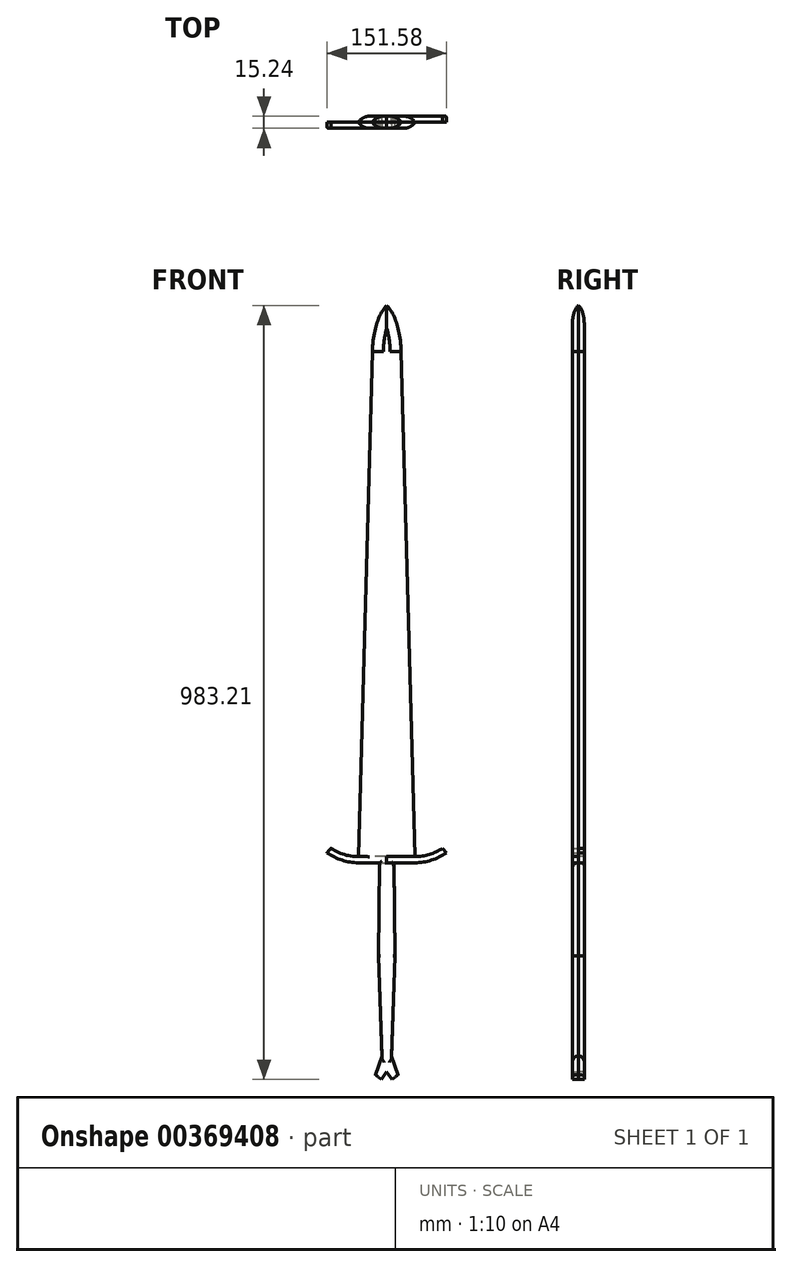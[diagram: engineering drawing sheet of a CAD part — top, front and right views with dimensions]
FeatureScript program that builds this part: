
annotation { "Feature Type Name" : "Feature", "Feature Type Description" : "" }
export const myFeature = defineFeature(function(context is Context, id is Id, definition is map)
    precondition{}
    {
        {
            var Q0;
            Q0=qCreatedBy(makeId("Front.planeOp"),FACE);
            var sketch = newSketch(context, id + "F0", { "sketchPlane" : qUnion([Q0])});
            skLineSegment(sketch, "E0", {"start": v(0, -570.47) * mm, "end": v(0, 382.75) * mm});
            skFitSpline(sketch, "E1", {"points": [v(0, 382.75) * mm, v(-11.14, 364.34) * mm, v(-18.35, 324.36) * mm], "startDerivative": vector(-35, -40.1) * mm, "endDerivative": vector(-2.28, -78.56) * mm});
            skLineSegment(sketch, "E2", {"start": v(-18.35, 324.36) * mm, "end": v(-35.93, -317.64) * mm});
            skLineSegment(sketch, "E3", {"start": v(0, -317.64) * mm, "end": v(-35.93, -317.64) * mm});
            skArc(sketch, "E4", {"start": v(-70.75, -306.94) * mm, "mid": v(-54.15, -314.9) * mm, "end": v(-35.93, -317.64) * mm});
            skLineSegment(sketch, "E5", {"start": v(-70.75, -306.94) * mm, "end": v(-75.79, -312.66) * mm});
            skLineSegment(sketch, "E6", {"start": v(0, -317.64) * mm, "end": v(0, -325.65) * mm});
            skArc(sketch, "E7", {"start": v(-75.79, -312.66) * mm, "mid": v(-56.83, -322.07) * mm, "end": v(-35.93, -325.43) * mm});
            skLineSegment(sketch, "E8", {"start": v(-35.93, -325.43) * mm, "end": v(0, -325.65) * mm});
            skLineSegment(sketch, "E9", {"start": v(-9.27, -325.6) * mm, "end": v(-10.18, -443.7) * mm});
            skLineSegment(sketch, "E10", {"start": v(-10.18, -443.7) * mm, "end": v(-6.03, -571.22) * mm});
            skLineSegment(sketch, "E11.MirrorCS", {"start": v(10.18, -443.7) * mm, "end": v(6.03, -571.22) * mm});
            skLineSegment(sketch, "E12.MirrorCS", {"start": v(9.27, -325.6) * mm, "end": v(10.18, -443.7) * mm});
            skLineSegment(sketch, "E13.MirrorCS", {"start": v(35.93, -325.43) * mm, "end": v(0, -325.65) * mm});
            skLineSegment(sketch, "E14.MirrorCS", {"start": v(0, -317.64) * mm, "end": v(35.93, -317.64) * mm});
            skLineSegment(sketch, "E15.MirrorCS", {"start": v(18.35, 324.36) * mm, "end": v(35.93, -317.64) * mm});
            skArc(sketch, "E16.MirrorCS", {"start": v(75.79, -312.66) * mm, "mid": v(56.83, -322.07) * mm, "end": v(35.93, -325.43) * mm});
            skArc(sketch, "E17.MirrorCS", {"start": v(70.75, -306.94) * mm, "mid": v(54.15, -314.9) * mm, "end": v(35.93, -317.64) * mm});
            skFitSpline(sketch, "E18.MirrorCS", {"points": [v(0, 382.75) * mm, v(11.14, 364.34) * mm, v(18.35, 324.36) * mm], "startDerivative": vector(35, -40.1) * mm, "endDerivative": vector(2.28, -78.56) * mm});
            skLineSegment(sketch, "E19", {"start": v(-6.03, -571.22) * mm, "end": v(-14.6, -594.67) * mm});
            skLineSegment(sketch, "E20", {"start": v(-14.6, -594.67) * mm, "end": v(-6.81, -600.46) * mm});
            skLineSegment(sketch, "E21", {"start": v(-6.81, -600.46) * mm, "end": v(0, -591.3) * mm});
            skLineSegment(sketch, "E22.MirrorCS", {"start": v(6.03, -571.22) * mm, "end": v(14.6, -594.67) * mm});
            skLineSegment(sketch, "E23.MirrorCS", {"start": v(14.6, -594.67) * mm, "end": v(6.81, -600.46) * mm});
            skLineSegment(sketch, "E24.MirrorCS", {"start": v(6.81, -600.46) * mm, "end": v(0, -591.3) * mm});
            skLineSegment(sketch, "E25.MirrorCS", {"start": v(70.75, -306.94) * mm, "end": v(75.79, -312.66) * mm});
            skSolve(sketch);
        }
        {
            var Q0;
            {var subQ0=sQuery(id+"F0.wireOp",EDGE,"E1");Q0=makeQuery(id+"F0.imprint","IMPRINT",FACE,{"disambiguationData":[TD([[makeQuery(id+"F0.imprint","IMPRINT",EDGE,{"derivedFrom":subQ0}),1.0]])]});}
            var Q1;
            {var subQ2=sQuery(id+"F0.wireOp",EDGE,"E14.MirrorCS");Q1=makeQuery(id+"F0.imprint","IMPRINT",FACE,{"disambiguationData":[TD([[makeQuery(id+"F0.imprint","IMPRINT",EDGE,{"derivedFrom":subQ2}),1.0]])]});}
            var Q2;
            Q2=makeQuery(id+"F0.imprint","IMPRINT",FACE,{"disambiguationData":[TD([[makeQuery(id+"F0.imprint","IMPRINT",EDGE,{"derivedFrom":sQuery(id+"F0.wireOp",EDGE,"E3")}),1.0]])]});
            var Q3;
            {var subQ1=sQuery(id+"F0.wireOp",EDGE,"E6");Q3=makeQuery(id+"F0.imprint","IMPRINT",FACE,{"disambiguationData":[TD([[makeQuery(id+"F0.imprint","IMPRINT",EDGE,{"derivedFrom":subQ1}),1.0]])]});}
            var Q4;
            {var subQ4=sQuery(id+"F0.wireOp",EDGE,"E9");Q4=makeQuery(id+"F0.imprint","IMPRINT",FACE,{"disambiguationData":[TD([[makeQuery(id+"F0.imprint","IMPRINT",EDGE,{"derivedFrom":subQ4}),1.0]])]});}
            extrude(context, id + "F1", {"entities" : qUnion([Q0, Q1, Q2, Q3, Q4]), "depth" : 7.62 * mm});
        }
        {
            var Q0;
            Q0=makeQuery(id+"F1.opExtrude","CAP_EDGE",EDGE,{"disambiguationData":[OSD([sQuery(id+"F0.wireOp",EDGE,"E15.MirrorCS")])],"isStart":false});
            var Q1;
            Q1=makeQuery(id+"F1.opExtrude","CAP_EDGE",EDGE,{"disambiguationData":[OSD([sQuery(id+"F0.wireOp",EDGE,"E2")])],"isStart":false});
            var Q2;
            Q2=makeQuery(id+"F1.opExtrude","CAP_EDGE",EDGE,{"disambiguationData":[OSD([sQuery(id+"F0.wireOp",EDGE,"E1")])],"isStart":false});
            var Q3;
            Q3=makeQuery(id+"F1.opExtrude","CAP_EDGE",EDGE,{"disambiguationData":[OSD([sQuery(id+"F0.wireOp",EDGE,"E18.MirrorCS")])],"isStart":false});
            fillet(context, id + "F2", {"entities" : qUnion([Q0, Q1, Q2, Q3]), "radius" : 16.56 * mm, "tangentPropagation" : true, "allowEdgeOverflow" : false});
        }
        {
            var Q0;
            Q0=makeQuery(id+"F1.opExtrude","CAP_EDGE",EDGE,{"disambiguationData":[OSD([sQuery(id+"F0.wireOp",EDGE,"E7")])],"isStart":false});
            var Q1;
            Q1=makeQuery(id+"F1.opExtrude","CAP_EDGE",EDGE,{"disambiguationData":[OSD([sQuery(id+"F0.wireOp",EDGE,"E8")])],"isStart":false});
            var Q2;
            Q2=makeQuery(id+"F1.opExtrude","CAP_EDGE",EDGE,{"disambiguationData":[OSD([sQuery(id+"F0.wireOp",EDGE,"E13.MirrorCS")])],"isStart":false});
            var Q3;
            Q3=makeQuery(id+"F1.opExtrude","CAP_EDGE",EDGE,{"disambiguationData":[OSD([sQuery(id+"F0.wireOp",EDGE,"E16.MirrorCS")])],"isStart":false});
            var Q4;
            Q4=makeQuery(id+"F1.opExtrude","CAP_EDGE",EDGE,{"disambiguationData":[OSD([sQuery(id+"F0.wireOp",EDGE,"E4")])],"isStart":false});
            var Q5;
            Q5=makeQuery(id+"F1.opExtrude","CAP_EDGE",EDGE,{"disambiguationData":[OSD([sQuery(id+"F0.wireOp",EDGE,"E17.MirrorCS")])],"isStart":false});
            fillet(context, id + "F3", {"entities" : qUnion([Q0, Q1, Q2, Q3, Q4, Q5]), "radius" : 1.84 * mm, "tangentPropagation" : true, "allowEdgeOverflow" : false});
        }
        {
            var Q0;
            Q0=makeQuery(id+"F1.opExtrude","CAP_EDGE",EDGE,{"disambiguationData":[OSD([sQuery(id+"F0.wireOp",EDGE,"E12.MirrorCS")])],"isStart":false});
            var Q1;
            Q1=makeQuery(id+"F1.opExtrude","CAP_EDGE",EDGE,{"disambiguationData":[OSD([sQuery(id+"F0.wireOp",EDGE,"E10")])],"isStart":false});
            var Q2;
            Q2=makeQuery(id+"F1.opExtrude","CAP_EDGE",EDGE,{"disambiguationData":[OSD([sQuery(id+"F0.wireOp",EDGE,"E11.MirrorCS")])],"isStart":false});
            var Q3;
            Q3=makeQuery(id+"F1.opExtrude","CAP_EDGE",EDGE,{"disambiguationData":[OSD([sQuery(id+"F0.wireOp",EDGE,"E9")])],"isStart":false});
            fillet(context, id + "F4", {"entities" : qUnion([Q0, Q1, Q2, Q3]), "radius" : 2.45 * mm, "tangentPropagation" : true, "allowEdgeOverflow" : false});
        }
        {
            var Q0;
            Q0=makeQuery(id+"F1.opExtrude","CAP_EDGE",EDGE,{"disambiguationData":[OSD([sQuery(id+"F0.wireOp",EDGE,"E19")])],"isStart":false});
            var Q1;
            Q1=makeQuery(id+"F1.opExtrude","CAP_EDGE",EDGE,{"disambiguationData":[OSD([sQuery(id+"F0.wireOp",EDGE,"E22.MirrorCS")])],"isStart":false});
            fillet(context, id + "F5", {"entities" : qUnion([Q0, Q1]), "radius" : 5.08 * mm, "tangentPropagation" : true, "allowEdgeOverflow" : false});
        }
        {
            var Q0;
            Q0=makeQuery(id+"F1.opExtrude","SWEPT_BODY",BODY,{"disambiguationData":[OSD([sQuery(id+"F0.wireOp",EDGE,"E1"),sQuery(id+"F0.wireOp",EDGE,"E2"),sQuery(id+"F0.wireOp",EDGE,"E4"),sQuery(id+"F0.wireOp",EDGE,"E5"),sQuery(id+"F0.wireOp",EDGE,"E7"),sQuery(id+"F0.wireOp",EDGE,"E8"),sQuery(id+"F0.wireOp",EDGE,"E9"),sQuery(id+"F0.wireOp",EDGE,"E10"),sQuery(id+"F0.wireOp",EDGE,"E11.MirrorCS"),sQuery(id+"F0.wireOp",EDGE,"E12.MirrorCS"),sQuery(id+"F0.wireOp",EDGE,"E13.MirrorCS"),sQuery(id+"F0.wireOp",EDGE,"E15.MirrorCS"),sQuery(id+"F0.wireOp",EDGE,"E16.MirrorCS"),sQuery(id+"F0.wireOp",EDGE,"E17.MirrorCS"),sQuery(id+"F0.wireOp",EDGE,"E18.MirrorCS"),sQuery(id+"F0.wireOp",EDGE,"E19"),sQuery(id+"F0.wireOp",EDGE,"E20"),sQuery(id+"F0.wireOp",EDGE,"E21"),sQuery(id+"F0.wireOp",EDGE,"E22.MirrorCS"),sQuery(id+"F0.wireOp",EDGE,"E23.MirrorCS"),sQuery(id+"F0.wireOp",EDGE,"E24.MirrorCS"),sQuery(id+"F0.wireOp",EDGE,"E25.MirrorCS")])]});
            transform(context, id + "F6", {"entities" : qUnion([Q0]), "transformType" : TransformType.COPY});
        }
        {
            var Q0;
            Q0=qCreatedBy(makeId("Front.planeOp"),FACE);
            var sketch = newSketch(context, id + "F7", { "sketchPlane" : qUnion([Q0])});
            skLineSegment(sketch, "E26", {"start": v(0, 10.39) * mm, "end": v(0, -6.33) * mm});
            skSolve(sketch);
        }
        {
            var Q0;
            Q0=makeQuery(id+"F6.opPattern","COPY",BODY,{"derivedFrom":makeQuery(id+"F1.opExtrude","SWEPT_BODY",BODY,{"disambiguationData":[OSD([sQuery(id+"F0.wireOp",EDGE,"E1"),sQuery(id+"F0.wireOp",EDGE,"E2"),sQuery(id+"F0.wireOp",EDGE,"E4"),sQuery(id+"F0.wireOp",EDGE,"E5"),sQuery(id+"F0.wireOp",EDGE,"E7"),sQuery(id+"F0.wireOp",EDGE,"E8"),sQuery(id+"F0.wireOp",EDGE,"E9"),sQuery(id+"F0.wireOp",EDGE,"E10"),sQuery(id+"F0.wireOp",EDGE,"E11.MirrorCS"),sQuery(id+"F0.wireOp",EDGE,"E12.MirrorCS"),sQuery(id+"F0.wireOp",EDGE,"E13.MirrorCS"),sQuery(id+"F0.wireOp",EDGE,"E15.MirrorCS"),sQuery(id+"F0.wireOp",EDGE,"E16.MirrorCS"),sQuery(id+"F0.wireOp",EDGE,"E17.MirrorCS"),sQuery(id+"F0.wireOp",EDGE,"E18.MirrorCS"),sQuery(id+"F0.wireOp",EDGE,"E19"),sQuery(id+"F0.wireOp",EDGE,"E20"),sQuery(id+"F0.wireOp",EDGE,"E21"),sQuery(id+"F0.wireOp",EDGE,"E22.MirrorCS"),sQuery(id+"F0.wireOp",EDGE,"E23.MirrorCS"),sQuery(id+"F0.wireOp",EDGE,"E24.MirrorCS"),sQuery(id+"F0.wireOp",EDGE,"E25.MirrorCS")])]}),"instanceName":"1"});
            var Q1;
            Q1=sQuery(id+"F7.wireOp",EDGE,"E26");
            transform(context, id + "F8", {"entities" : qUnion([Q0]), "transformType" : TransformType.ROTATION, "transformAxis" : qUnion([Q1]), "angle" : 180 * degree, "makeCopy" : false});
        }
    });
